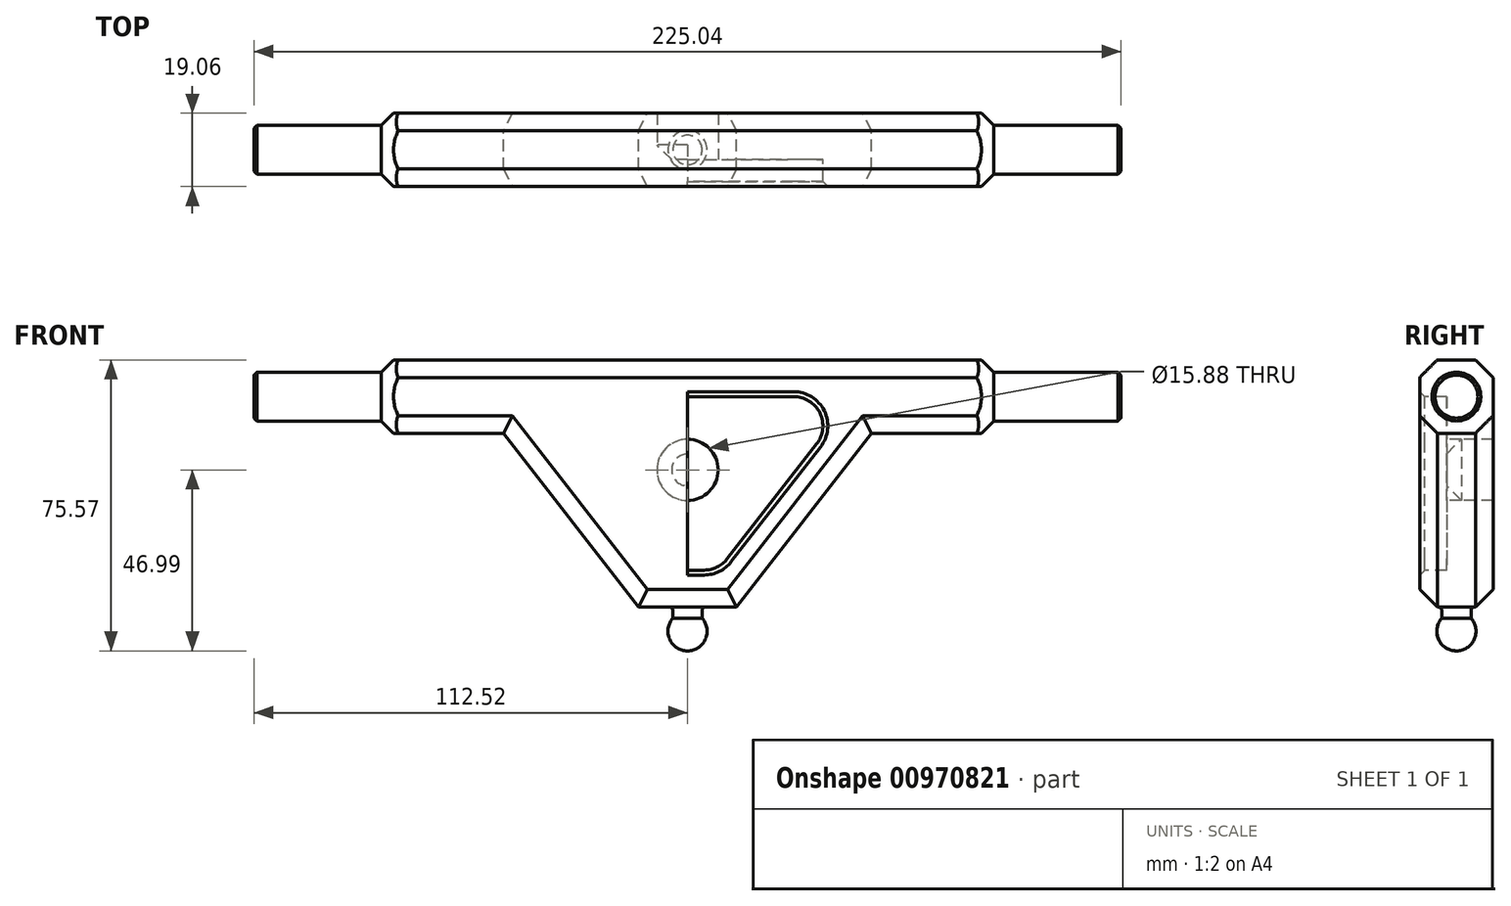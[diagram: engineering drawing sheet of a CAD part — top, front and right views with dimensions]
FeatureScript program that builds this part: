
annotation { "Feature Type Name" : "Feature", "Feature Type Description" : "" }
export const myFeature = defineFeature(function(context is Context, id is Id, definition is map)
    precondition{}
    {
        {
            var Q0;
            Q0=qCreatedBy(makeId("Front.planeOp"),FACE);
            var sketch = newSketch(context, id + "F0", { "sketchPlane" : qUnion([Q0])});
            skLineSegment(sketch, "E0", {"start": v(0, 0) * mm, "end": v(0, 64.14) * mm});
            skLineSegment(sketch, "E1", {"start": v(0, 64.14) * mm, "end": v(79.5, 64.14) * mm});
            skLineSegment(sketch, "E2", {"start": v(79.5, 64.14) * mm, "end": v(79.5, 45.09) * mm});
            skLineSegment(sketch, "E3", {"start": v(12.7, 0) * mm, "end": v(0, 0) * mm});
            skLineSegment(sketch, "E4", {"start": v(79.5, 45.09) * mm, "end": v(47.75, 45.09) * mm});
            skLineSegment(sketch, "E5", {"start": v(47.75, 45.09) * mm, "end": v(12.7, 0) * mm});
            skLineSegment(sketch, "E6", {"start": v(0, 54.61) * mm, "end": v(79.5, 54.61) * mm, "construction": true});
            skLineSegment(sketch, "E7", {"start": v(0, 64.14) * mm, "end": v(0, 80.96) * mm, "construction": true});
            skSolve(sketch);
        }
        {
            var Q0;
            Q0 = qSketchRegion(id + "F0", true);
            extrude(context, id + "F1", {"entities" : qUnion([Q0]), "depth" : 9.52 * mm, "offsetDistance" : 25.4 * mm});
        }
        {
            var Q0;
            Q0=makeQuery(id+"F1.opExtrude","SWEPT_BODY",BODY,{"disambiguationData":[OSD([sQuery(id+"F0.wireOp",EDGE,"E0"),sQuery(id+"F0.wireOp",EDGE,"E1"),sQuery(id+"F0.wireOp",EDGE,"E2"),sQuery(id+"F0.wireOp",EDGE,"E3"),sQuery(id+"F0.wireOp",EDGE,"E4"),sQuery(id+"F0.wireOp",EDGE,"E5")])]});
            var Q1;
            Q1=qCreatedBy(makeId("Front.planeOp"),FACE);
            mirror(context, id + "F2", {"operationType" : NewBodyOperationType.ADD, "entities" : qUnion([Q0]), "mirrorPlane" : qUnion([Q1])});
        }
        {
            var Q0;
            Q0=qCreatedBy(makeId("Front.planeOp"),FACE);
            var sketch = newSketch(context, id + "F3", { "sketchPlane" : qUnion([Q0])});
            skLineSegment(sketch, "E8", {"start": v(79.5, 54.61) * mm, "end": v(79.5, 73.66) * mm});
            skLineSegment(sketch, "E9", {"start": v(79.5, 73.66) * mm, "end": v(66.8, 73.66) * mm});
            skLineSegment(sketch, "E10", {"start": v(66.8, 73.66) * mm, "end": v(79.5, 60.96) * mm});
            skLineSegment(sketch, "E11.0", {"start": v(0, 54.61) * mm, "end": v(79.5, 54.61) * mm, "construction": true});
            skSolve(sketch);
        }
        {
            var Q0;
            Q0 = qSketchRegion(id + "F3", true);
            var Q1;
            Q1=sQuery(id+"F3.wireOp",EDGE,"E11.0");
            revolve(context, id + "F4", {"operationType" : NewBodyOperationType.REMOVE, "surfaceOperationType" : NewSurfaceOperationType.NEW, "entities" : qUnion([Q0]), "axis" : qUnion([Q1]), "revolveType" : RevolveType.FULL, "oppositeDirection" : true});
        }
        {
            var Q0;
            Q0=qCreatedBy(makeId("Right.planeOp"),FACE);
            var sketch = newSketch(context, id + "F5", { "sketchPlane" : qUnion([Q0])});
            skSolve(sketch);
        }
        {
            var Q0;
            Q0 = qSketchRegion(id + "F5", true);
            var Q1;
            {var subQ0=makeQuery(id+"F1.opExtrude","SWEPT_FACE",FACE,{"disambiguationData":[OSD([sQuery(id+"F0.wireOp",EDGE,"E2")])]});Q1=makeQuery(id+"F2.boolean.opBoolean","MERGE",FACE,{"derivedFrom":[subQ0,makeQuery(id+"F2.opPattern","COPY",FACE,{"derivedFrom":subQ0,"instanceName":"1"})]});}
            extrude(context, id + "F6", {"entities" : qUnion([Q0, Q1]), "operationType" : NewBodyOperationType.ADD, "depth" : 33.02 * mm, "offsetDistance" : 25.4 * mm});
        }
        {
            var Q0;
            Q0=qCreatedBy(makeId("Right.planeOp"),FACE);
            var sketch = newSketch(context, id + "F7", { "sketchPlane" : qUnion([Q0])});
            skLineSegment(sketch, "E12", {"start": v(0, 52.13) * mm, "end": v(0, 0) * mm, "construction": true});
            skArc(sketch, "E13", {"start": v(-3.81, -2.99) * mm, "mid": v(-4.63, -8.44) * mm, "end": v(0, -11.43) * mm});
            skLineSegment(sketch, "E14.0", {"start": v(-9.53, 0) * mm, "end": v(-4.83, 0) * mm});
            skLineSegment(sketch, "E15", {"start": v(-3.81, -1.02) * mm, "end": v(-3.81, -2.99) * mm});
            skPoint(sketch, "E16.newPointA", {"position": v(9.52, 0) * mm});
            skArc(sketch, "E16.filletArc", {"start": v(-3.81, -1.02) * mm, "mid": v(-4.1, -0.3) * mm, "end": v(-4.83, 0) * mm});
            skLineSegment(sketch, "E17", {"start": v(0, -6.35) * mm, "end": v(0, -11.43) * mm});
            skLineSegment(sketch, "E18", {"start": v(0, -1.27) * mm, "end": v(0, -6.35) * mm});
            skLineSegment(sketch, "E19", {"start": v(0, 0) * mm, "end": v(-4.83, 0) * mm});
            skLineSegment(sketch, "E20", {"start": v(0, 0) * mm, "end": v(0, -1.27) * mm});
            skSolve(sketch);
        }
        {
            var Q0;
            Q0 = qSketchRegion(id + "F7", true);
            var Q1;
            Q1=sQuery(id+"F7.wireOp",EDGE,"E18");
            revolve(context, id + "F8", {"operationType" : NewBodyOperationType.ADD, "surfaceOperationType" : NewSurfaceOperationType.NEW, "entities" : qUnion([Q0]), "axis" : qUnion([Q1]), "revolveType" : RevolveType.FULL});
        }
        {
            var Q0;
            Q0=makeQuery(id+"F1.opExtrude","SWEPT_BODY",BODY,{"disambiguationData":[OSD([sQuery(id+"F0.wireOp",EDGE,"E0"),sQuery(id+"F0.wireOp",EDGE,"E1"),sQuery(id+"F0.wireOp",EDGE,"E2"),sQuery(id+"F0.wireOp",EDGE,"E3"),sQuery(id+"F0.wireOp",EDGE,"E4"),sQuery(id+"F0.wireOp",EDGE,"E5")])]});
            var Q1;
            Q1=qCreatedBy(makeId("Right.planeOp"),FACE);
            mirror(context, id + "F9", {"operationType" : NewBodyOperationType.ADD, "entities" : qUnion([Q0]), "mirrorPlane" : qUnion([Q1])});
        }
        {
            var Q0;
            {var subQ0=makeQuery(id+"F1.opExtrude","CAP_FACE",FACE,{"disambiguationData":[OSD([sQuery(id+"F0.wireOp",EDGE,"E0"),sQuery(id+"F0.wireOp",EDGE,"E1"),sQuery(id+"F0.wireOp",EDGE,"E2"),sQuery(id+"F0.wireOp",EDGE,"E3"),sQuery(id+"F0.wireOp",EDGE,"E4"),sQuery(id+"F0.wireOp",EDGE,"E5")])],"isStart":false});Q0=makeQuery(id+"F9.boolean.opBoolean","MERGE",FACE,{"derivedFrom":[subQ0,makeQuery(id+"F9.opPattern","COPY",FACE,{"derivedFrom":subQ0,"instanceName":"1"})]});}
            var sketch = newSketch(context, id + "F10", { "sketchPlane" : qUnion([Q0])});
            skLineSegment(sketch, "E21.0", {"start": v(43.1, 54.61) * mm, "end": v(43.1, 54.61) * mm});
            skLineSegment(sketch, "E22.0", {"start": v(0, 54.61) * mm, "end": v(43.1, 54.61) * mm});
            skLineSegment(sketch, "E23", {"start": v(0, 9.54) * mm, "end": v(8.05, 9.54) * mm});
            skLineSegment(sketch, "E24", {"start": v(0, 54.61) * mm, "end": v(0, 9.54) * mm});
            skLineSegment(sketch, "E25", {"start": v(43.1, 54.61) * mm, "end": v(8.05, 9.54) * mm});
            skSolve(sketch);
        }
        {
            var Q0;
            Q0 = qSketchRegion(id + "F10", true);
            extrude(context, id + "F11", {"entities" : qUnion([Q0]), "operationType" : NewBodyOperationType.REMOVE, "oppositeDirection" : true, "depth" : 7 * mm, "offsetDistance" : 25.4 * mm});
        }
        {
            var Q0;
            Q0=makeQuery(id+"F11.boolean.opBoolean","COPY",EDGE,{"derivedFrom":makeQuery(id+"F11.opExtrude","SWEPT_EDGE",EDGE,{"disambiguationData":[OSD([sQuery(id+"F10.wireOp",EDGE,"E22.0"),sQuery(id+"F10.wireOp",EDGE,"E25")])]})});
            var Q1;
            Q1=makeQuery(id+"F11.boolean.opBoolean","COPY",EDGE,{"derivedFrom":makeQuery(id+"F11.opExtrude","SWEPT_EDGE",EDGE,{"disambiguationData":[OSD([sQuery(id+"F10.wireOp",EDGE,"E23"),sQuery(id+"F10.wireOp",EDGE,"E25")])]})});
            fillet(context, id + "F12", {"entities" : qUnion([Q0, Q1]), "radius" : 7.62 * mm, "tangentPropagation" : true, "allowEdgeOverflow" : false});
        }
        {
            var Q0;
            Q0=makeQuery(id+"F11.boolean.opBoolean","COPY",EDGE,{"derivedFrom":makeQuery(id+"F11.opExtrude","CAP_EDGE",EDGE,{"disambiguationData":[OSD([sQuery(id+"F10.wireOp",EDGE,"E22.0")])],"isStart":true})});
            var Q1;
            {var subQ0=makeQuery(id+"F1.opExtrude","CAP_FACE",FACE,{"disambiguationData":[OSD([sQuery(id+"F0.wireOp",EDGE,"E0"),sQuery(id+"F0.wireOp",EDGE,"E1"),sQuery(id+"F0.wireOp",EDGE,"E2"),sQuery(id+"F0.wireOp",EDGE,"E3"),sQuery(id+"F0.wireOp",EDGE,"E4"),sQuery(id+"F0.wireOp",EDGE,"E5")])],"isStart":false});Q1=makeQuery(id+"F12.opFillet","BLEND_EDGE",EDGE,{"blendedFrom":[makeQuery(id+"F11.boolean.opBoolean","COPY",EDGE,{"derivedFrom":makeQuery(id+"F11.opExtrude","SWEPT_EDGE",EDGE,{"disambiguationData":[OSD([sQuery(id+"F10.wireOp",EDGE,"E22.0"),sQuery(id+"F10.wireOp",EDGE,"E25")])]})}),makeQuery(id+"F9.boolean.opBoolean","MERGE",FACE,{"derivedFrom":[subQ0,makeQuery(id+"F9.opPattern","COPY",FACE,{"derivedFrom":subQ0,"instanceName":"1"})]})],"blendedInto":[makeQuery(id+"F9.boolean.opBoolean","MERGE",FACE,{"derivedFrom":[subQ0,makeQuery(id+"F9.opPattern","COPY",FACE,{"derivedFrom":subQ0,"instanceName":"1"})]})]});}
            var Q2;
            Q2=makeQuery(id+"F11.boolean.opBoolean","COPY",EDGE,{"derivedFrom":makeQuery(id+"F11.opExtrude","CAP_EDGE",EDGE,{"disambiguationData":[OSD([sQuery(id+"F10.wireOp",EDGE,"E25")])],"isStart":true})});
            var Q3;
            {var subQ0=makeQuery(id+"F1.opExtrude","CAP_FACE",FACE,{"disambiguationData":[OSD([sQuery(id+"F0.wireOp",EDGE,"E0"),sQuery(id+"F0.wireOp",EDGE,"E1"),sQuery(id+"F0.wireOp",EDGE,"E2"),sQuery(id+"F0.wireOp",EDGE,"E3"),sQuery(id+"F0.wireOp",EDGE,"E4"),sQuery(id+"F0.wireOp",EDGE,"E5")])],"isStart":false});Q3=makeQuery(id+"F12.opFillet","BLEND_EDGE",EDGE,{"blendedFrom":[makeQuery(id+"F11.boolean.opBoolean","COPY",EDGE,{"derivedFrom":makeQuery(id+"F11.opExtrude","SWEPT_EDGE",EDGE,{"disambiguationData":[OSD([sQuery(id+"F10.wireOp",EDGE,"E23"),sQuery(id+"F10.wireOp",EDGE,"E25")])]})}),makeQuery(id+"F9.boolean.opBoolean","MERGE",FACE,{"derivedFrom":[subQ0,makeQuery(id+"F9.opPattern","COPY",FACE,{"derivedFrom":subQ0,"instanceName":"1"})]})],"blendedInto":[makeQuery(id+"F9.boolean.opBoolean","MERGE",FACE,{"derivedFrom":[subQ0,makeQuery(id+"F9.opPattern","COPY",FACE,{"derivedFrom":subQ0,"instanceName":"1"})]})]});}
            var Q4;
            Q4=makeQuery(id+"F11.boolean.opBoolean","COPY",EDGE,{"derivedFrom":makeQuery(id+"F11.opExtrude","CAP_EDGE",EDGE,{"disambiguationData":[OSD([sQuery(id+"F10.wireOp",EDGE,"E23")])],"isStart":true})});
            chamfer(context, id + "F13", {"entities" : qUnion([Q0, Q1, Q2, Q3, Q4]), "width" : 1.27 * mm, "tangentPropagation" : true});
        }
        {
            var Q0;
            {var subQ0=sQuery(id+"F10.wireOp",EDGE,"E25");var subQ1=sQuery(id+"F10.wireOp",EDGE,"E24");var subQ2=sQuery(id+"F10.wireOp",EDGE,"E23");var subQ3=sQuery(id+"F10.wireOp",EDGE,"E22.0");Q0=makeQuery(id+"FN1GpqA03T7QDDV_1.1.F11.boolean.opBoolean","MERGE",FACE,{"derivedFrom":[makeQuery(id+"F11.boolean.opBoolean","COPY",FACE,{"derivedFrom":makeQuery(id+"F11.opExtrude","CAP_FACE",FACE,{"disambiguationData":[OSD([subQ3,subQ2,subQ1,subQ0])],"isStart":false})})],"fromTools":[makeQuery(id+"FN1GpqA03T7QDDV_1.1.F11.opExtrude","CAP_FACE",FACE,{"disambiguationData":[OSD([subQ3,subQ2,subQ1,subQ0])],"isStart":false})]});}
            var sketch = newSketch(context, id + "F14", { "sketchPlane" : qUnion([Q0])});
            skCircle(sketch, "E26", {"center": v(0, 35.56) * mm, "radius": 7.94 * mm});
            skSolve(sketch);
        }
        {
            var Q0;
            Q0=makeQuery(id+"F14.imprint","IMPRINT",FACE,{"disambiguationData":[TD([[makeQuery(id+"F14.imprint","IMPRINT",EDGE,{"derivedFrom":sQuery(id+"F14.wireOp",EDGE,"E26")}),1.0]])]});
            var Q1;
            Q1=sQuery(id+"F14.wireOp",EDGE,"E26");
            extrude(context, id + "F15", {"entities" : qUnion([Q0]), "operationType" : NewBodyOperationType.REMOVE, "surfaceEntities" : qUnion([Q1]), "endBound" : BoundingType.THROUGH_ALL, "oppositeDirection" : true, "depth" : 25.4 * mm, "offsetDistance" : 25.4 * mm});
        }
        {
            var Q0;
            Q0=makeQuery(id+"F15.boolean.opBoolean","COPY",EDGE,{"derivedFrom":makeQuery(id+"F15.opExtrude","CAP_EDGE",EDGE,{"disambiguationData":[OSD([sQuery(id+"F14.wireOp",EDGE,"E26")])],"isStart":true})});
            chamfer(context, id + "F16", {"entities" : qUnion([Q0]), "width" : 3.8 * mm, "tangentPropagation" : true});
        }
        {
            var Q0;
            Q0=makeQuery(id+"F6.opExtrude","CAP_EDGE",EDGE,{"disambiguationData":[OSD([sQuery(id+"F3.wireOp",EDGE,"E8"),sQuery(id+"F3.wireOp",EDGE,"E10")])],"isStart":false});
            var Q1;
            Q1=makeQuery(id+"F9.opPattern","COPY",EDGE,{"derivedFrom":makeQuery(id+"F6.opExtrude","CAP_EDGE",EDGE,{"disambiguationData":[OSD([sQuery(id+"F3.wireOp",EDGE,"E8"),sQuery(id+"F3.wireOp",EDGE,"E10")])],"isStart":false}),"instanceName":"1"});
            chamfer(context, id + "F17", {"entities" : qUnion([Q0, Q1]), "width" : 0.76 * mm, "tangentPropagation" : true});
        }
        {
            var Q0;
            {var subQ0=makeQuery(id+"F1.opExtrude","CAP_EDGE",EDGE,{"disambiguationData":[OSD([sQuery(id+"F0.wireOp",EDGE,"E1")])],"isStart":false});Q0=makeQuery(id+"F9.boolean.opBoolean","MERGE",EDGE,{"derivedFrom":[subQ0,makeQuery(id+"F9.opPattern","COPY",EDGE,{"derivedFrom":subQ0,"instanceName":"1"})]});}
            var Q1;
            Q1=makeQuery(id+"F1.opExtrude","CAP_EDGE",EDGE,{"disambiguationData":[OSD([sQuery(id+"F0.wireOp",EDGE,"E4")])],"isStart":false});
            var Q2;
            Q2=makeQuery(id+"F1.opExtrude","CAP_EDGE",EDGE,{"disambiguationData":[OSD([sQuery(id+"F0.wireOp",EDGE,"E5")])],"isStart":false});
            var Q3;
            {var subQ0=makeQuery(id+"F1.opExtrude","CAP_EDGE",EDGE,{"disambiguationData":[OSD([sQuery(id+"F0.wireOp",EDGE,"E3")])],"isStart":false});Q3=makeQuery(id+"F9.boolean.opBoolean","MERGE",EDGE,{"derivedFrom":[subQ0,makeQuery(id+"F9.opPattern","COPY",EDGE,{"derivedFrom":subQ0,"instanceName":"1"})]});}
            var Q4;
            Q4=makeQuery(id+"F9.opPattern","COPY",EDGE,{"derivedFrom":makeQuery(id+"F1.opExtrude","CAP_EDGE",EDGE,{"disambiguationData":[OSD([sQuery(id+"F0.wireOp",EDGE,"E5")])],"isStart":false}),"instanceName":"1"});
            var Q5;
            Q5=makeQuery(id+"F9.opPattern","COPY",EDGE,{"derivedFrom":makeQuery(id+"F1.opExtrude","CAP_EDGE",EDGE,{"disambiguationData":[OSD([sQuery(id+"F0.wireOp",EDGE,"E4")])],"isStart":false}),"instanceName":"1"});
            var Q6;
            {var subQ0=makeQuery(id+"F2.opPattern","COPY",EDGE,{"derivedFrom":makeQuery(id+"F1.opExtrude","CAP_EDGE",EDGE,{"disambiguationData":[OSD([sQuery(id+"F0.wireOp",EDGE,"E1")])],"isStart":false}),"instanceName":"1"});Q6=makeQuery(id+"F9.boolean.opBoolean","MERGE",EDGE,{"derivedFrom":[subQ0,makeQuery(id+"F9.opPattern","COPY",EDGE,{"derivedFrom":subQ0,"instanceName":"1"})]});}
            var Q7;
            Q7=makeQuery(id+"F9.opPattern","COPY",EDGE,{"derivedFrom":makeQuery(id+"F2.opPattern","COPY",EDGE,{"derivedFrom":makeQuery(id+"F1.opExtrude","CAP_EDGE",EDGE,{"disambiguationData":[OSD([sQuery(id+"F0.wireOp",EDGE,"E4")])],"isStart":false}),"instanceName":"1"}),"instanceName":"1"});
            var Q8;
            Q8=makeQuery(id+"F2.opPattern","COPY",EDGE,{"derivedFrom":makeQuery(id+"F1.opExtrude","CAP_EDGE",EDGE,{"disambiguationData":[OSD([sQuery(id+"F0.wireOp",EDGE,"E5")])],"isStart":false}),"instanceName":"1"});
            var Q9;
            Q9=makeQuery(id+"F2.opPattern","COPY",EDGE,{"derivedFrom":makeQuery(id+"F1.opExtrude","CAP_EDGE",EDGE,{"disambiguationData":[OSD([sQuery(id+"F0.wireOp",EDGE,"E4")])],"isStart":false}),"instanceName":"1"});
            var Q10;
            {var subQ0=makeQuery(id+"F2.opPattern","COPY",EDGE,{"derivedFrom":makeQuery(id+"F1.opExtrude","CAP_EDGE",EDGE,{"disambiguationData":[OSD([sQuery(id+"F0.wireOp",EDGE,"E3")])],"isStart":false}),"instanceName":"1"});Q10=makeQuery(id+"F9.boolean.opBoolean","MERGE",EDGE,{"derivedFrom":[subQ0,makeQuery(id+"F9.opPattern","COPY",EDGE,{"derivedFrom":subQ0,"instanceName":"1"})]});}
            var Q11;
            Q11=makeQuery(id+"F9.opPattern","COPY",EDGE,{"derivedFrom":makeQuery(id+"F2.opPattern","COPY",EDGE,{"derivedFrom":makeQuery(id+"F1.opExtrude","CAP_EDGE",EDGE,{"disambiguationData":[OSD([sQuery(id+"F0.wireOp",EDGE,"E5")])],"isStart":false}),"instanceName":"1"}),"instanceName":"1"});
            chamfer(context, id + "F18", {"entities" : qUnion([Q0, Q1, Q2, Q3, Q4, Q5, Q6, Q7, Q8, Q9, Q10, Q11]), "width" : 4.57 * mm, "tangentPropagation" : true});
        }
    });
